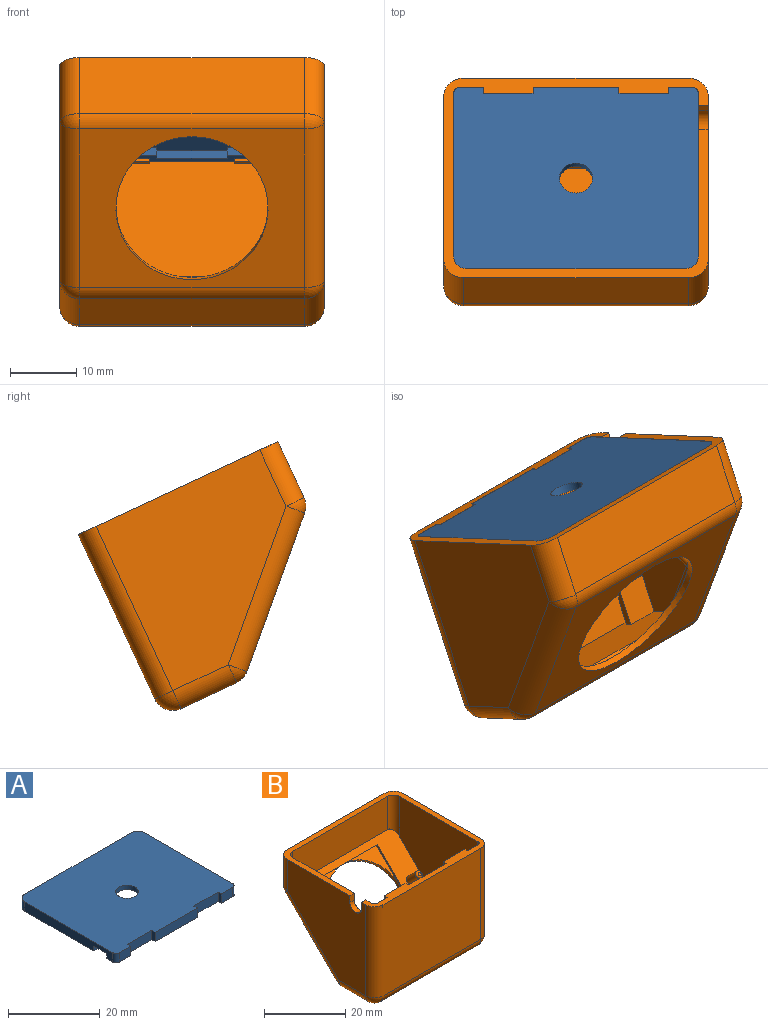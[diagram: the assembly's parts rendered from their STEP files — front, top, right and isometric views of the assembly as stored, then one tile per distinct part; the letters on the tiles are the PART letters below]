
ASSEMBLY  parts=2 mates=1
PART A: 37 faces, bbox 37x30.3x2.5 mm
  f0: plane 1.8x1.3mm, normal (1,0,0), area 2.3mm2, adj f17,f22,f33,f34
  f1: plane 33x2.5mm, normal (0,1,0), area 82.5mm2, adj f2,f16,f17,f18
  f2: cylinder r=2mm len=2.5mm, axis (0,0,1), area 7.9mm2, adj f1,f3,f17,f18
  f3: plane 27.3x2.5mm, normal (-1,0,0), area 63mm2, adj f2,f4,f17,f18,f33,f34,f35
  f4: cylinder r=1mm len=2.5mm, axis (0,0,1), area 3.9mm2, adj f3,f5,f17,f18
  f5: plane 3.5x2.5mm, normal (0,-1,0), area 8.7mm2, adj f4,f6,f17,f18
  f6: plane 2.5x1mm, normal (1,0,0), area 2.5mm2, adj f5,f7,f17,f18
  f7: plane 7.5x2.5mm, normal (0,-1,0), area 18.8mm2, adj f6,f8,f17,f18
  f8: plane 2.5x1mm, normal (-1,0,0), area 2.5mm2, adj f7,f9,f17,f18
  f9: plane 13x2.5mm, normal (0,-1,0), area 32.5mm2, adj f8,f10,f17,f18
  f10: plane 2.5x1mm, normal (1,0,0), area 2.5mm2, adj f9,f11,f17,f18
  f11: plane 7.5x2.5mm, normal (0,-1,0), area 18.8mm2, adj f10,f12,f17,f18
  f12: plane 2.5x1mm, normal (-1,0,0), area 2.5mm2, adj f11,f13,f17,f18
  f13: plane 3.5x2.5mm, normal (0,-1,0), area 8.7mm2, adj f12,f14,f17,f18
  f14: cylinder r=1mm len=2.5mm, axis (0,0,1), area 3.9mm2, adj f13,f15,f17,f18
  f15: plane 27.3x2.5mm, normal (1,0,0), area 68.2mm2, adj f14,f16,f17,f18
  f16: cylinder r=2mm len=2.5mm, axis (0,0,1), area 7.9mm2, adj f1,f15,f17,f18
  f17: plane 37x30.3mm, normal (0,0,-1), area 153.9mm2, adj f0,f1,f2,f3,f4,f5,f6,f7
  f18: plane 37x30.3mm, normal (0,0,1), area 1084.3mm2, adj f1,f2,f3,f4,f5,f6,f7,f8
  f19: plane 33x1.3mm, normal (0,-1,0), area 42.9mm2, adj f17,f20,f32,f33
  f20: cylinder r=0.8mm len=1.3mm, axis (0,0,1), area 1.6mm2, adj f17,f19,f21,f33
  f21: plane 21.3x1.3mm, normal (1,0,0), area 27.7mm2, adj f17,f20,f33,f35
  f22: plane 2.1x1.3mm, normal (0,1,0), area 2.7mm2, adj f0,f17,f23,f33
  f23: plane 1.3x1mm, normal (-1,0,0), area 1.3mm2, adj f17,f22,f24,f33
  f24: plane 9.9x1.3mm, normal (0,1,0), area 12.9mm2, adj f17,f23,f25,f33
  f25: plane 1.3x1mm, normal (1,0,0), area 1.3mm2, adj f17,f24,f26,f33
  f26: plane 10.6x1.3mm, normal (0,1,0), area 13.8mm2, adj f17,f25,f27,f33
  f27: plane 1.3x1mm, normal (-1,0,0), area 1.3mm2, adj f17,f26,f28,f33
  f28: plane 9.9x1.3mm, normal (0,1,0), area 12.9mm2, adj f17,f27,f29,f33
  f29: plane 1.3x1mm, normal (1,0,0), area 1.3mm2, adj f17,f28,f30,f33
  f30: plane 2.1x1.3mm, normal (0,1,0), area 2.7mm2, adj f17,f29,f31,f33
  f31: plane 27.1x1.3mm, normal (-1,0,0), area 35.2mm2, adj f17,f30,f32,f33
  f32: cylinder r=0.8mm len=1.3mm, axis (0,0,1), area 1.6mm2, adj f17,f19,f31,f33
  f33: plane 35.8x27.9mm, normal (0,0,-1), area 930.4mm2, adj f0,f3,f19,f20,f21,f22,f23,f24
  f34: plane 1.3x1.2mm, normal (0,1,0), area 1.6mm2, adj f0,f3,f17,f33
  f35: plane 1.3x1.2mm, normal (0,-1,0), area 1.6mm2, adj f3,f17,f21,f33
  f36: cylinder r=2.5mm len=5mm, axis (0,0,-1), area 18.8mm2, adj f18,f33
PART B: 68 faces, bbox 40x33.3x30.4 mm
  f0: plane 40x33.3mm, normal (0,0,1), area 214.3mm2, adj f2,f5,f8,f9,f10,f11,f12,f13
  f1: plane 37x11.38mm, normal (0,0,1), area 412.6mm2, adj f2,f4,f11,f13,f47,f48,f49,f50
  f2: plane 28.91x27.3mm, normal (1,0,0), area 626.6mm2, adj f0,f1,f4,f45,f48,f61,f63,f64
  f3: cylinder r=11.5mm len=23mm, axis (0,0.71,-0.71), area 72.3mm2, adj f7,f16,f19,f20,f21
  f4: plane 37x18.92mm, normal (0,-0.71,0.71), area 452.9mm2, adj f1,f2,f12,f13,f14,f15,f17,f18
  f5: plane 34x27.41mm, normal (0,-1,0), area 931.8mm2, adj f0,f38,f41,f44
  f6: plane 34x9.26mm, normal (0,0,-1), area 314.8mm2, adj f34,f39,f40,f44
  f7: plane 34x18.04mm, normal (0,0.71,-0.71), area 452mm2, adj f3,f29,f33,f34,f35
  f8: plane 34x9.36mm, normal (0,1,0), area 318.4mm2, adj f0,f28,f29,f30
  f9: plane 27.41x27.3mm, normal (1,0,0), area 585.4mm2, adj f0,f28,f33,f38,f39
  f10: plane 27.41x27.3mm, normal (-1,0,0), area 571.1mm2, adj f0,f30,f35,f40,f41,f63,f64,f65
  f11: plane 35x28.91mm, normal (0,1,0), area 968.1mm2, adj f0,f1,f53,f54,f55,f57,f58,f59
  f12: plane 33x9.99mm, normal (0,-1,0), area 329.5mm2, adj f0,f4,f45,f46
  f13: plane 28.91x27.3mm, normal (-1,0,0), area 640.9mm2, adj f0,f1,f4,f46,f51,f62,f66
  f14: plane 16.62x16.62mm, normal (-1,0,0), area 11.5mm2, adj f4,f15,f16,f17,f21
  f15: plane 23x0.35mm, normal (0,0.71,0.71), area 11.5mm2, adj f4,f14,f16,f18,f20
  f16: plane 11.5x8.13mm, normal (0,-0.71,0.71), area 28.4mm2, adj f3,f14,f15
  f17: plane 23x0.35mm, normal (0,-0.71,-0.71), area 11.5mm2, adj f4,f14,f18,f19,f21
  f18: plane 16.62x16.62mm, normal (1,0,0), area 11.5mm2, adj f4,f15,f17,f19,f20
  f19: plane 11.5x8.13mm, normal (0,-0.71,0.71), area 28.4mm2, adj f3,f17,f18
  f20: plane 11.5x8.13mm, normal (0,-0.71,0.71), area 28.4mm2, adj f3,f15,f18
  f21: plane 11.5x8.13mm, normal (0,-0.71,0.71), area 28.4mm2, adj f3,f14,f17
  f22: cylinder r=0.95mm len=4.53mm, axis (0,0.71,-0.71), area 26.9mm2, adj f4,f26
  f23: plane 0.9x0.64mm, normal (0,-0.71,0.71), area 0.6mm2, adj f26
  f24: cylinder r=0.95mm len=4.53mm, axis (0,0.71,-0.71), area 26.9mm2, adj f4,f27
  f25: plane 0.9x0.64mm, normal (0,-0.71,0.71), area 0.6mm2, adj f27
  f26: torus R=0.45mm, axis (0,-0.71,0.71), area 3.8mm2, adj f22,f23
  f27: torus R=0.45mm, axis (0,-0.71,0.71), area 3.8mm2, adj f24,f25
  f28: cylinder r=3mm len=9.36mm, axis (0,0,-1), area 44.1mm2, adj f0,f8,f9,f31
  f29: cylinder r=3mm len=34mm, axis (-1,0,0), area 80.1mm2, adj f7,f8,f31,f32
  f30: cylinder r=3mm len=9.36mm, axis (0,0,1), area 44.1mm2, adj f0,f8,f10,f32
  f31: sphere r=3mm, area 7.1mm2, adj f28,f29,f33
  f32: sphere r=3mm, area 7.1mm2, adj f29,f30,f35
  f33: cylinder r=3mm len=20.16mm, axis (0,-0.71,-0.71), area 120.2mm2, adj f7,f9,f31,f36
  f34: cylinder r=3mm len=34mm, axis (-1,0,0), area 80.1mm2, adj f6,f7,f36,f37
  f35: cylinder r=3mm len=20.16mm, axis (0,0.71,0.71), area 120.2mm2, adj f7,f10,f32,f37
  f36: sphere r=3mm, area 7.1mm2, adj f33,f34,f39
  f37: sphere r=3mm, area 7.1mm2, adj f34,f35,f40
  f38: cylinder r=3mm len=27.41mm, axis (0,0,1), area 129.1mm2, adj f0,f5,f9,f42
  f39: cylinder r=3mm len=9.26mm, axis (0,-1,0), area 43.6mm2, adj f6,f9,f36,f42
  f40: cylinder r=3mm len=9.26mm, axis (0,1,0), area 43.6mm2, adj f6,f10,f37,f43
  f41: cylinder r=3mm len=27.41mm, axis (0,0,-1), area 129.1mm2, adj f0,f5,f10,f43
  f42: sphere r=3mm, area 14.1mm2, adj f38,f39,f44
  f43: sphere r=3mm, area 14.1mm2, adj f40,f41,f44
  f44: cylinder r=3mm len=34mm, axis (-1,0,0), area 160.2mm2, adj f5,f6,f42,f43
  f45: cylinder r=2mm len=11.99mm, axis (0,0,-1), area 33.7mm2, adj f0,f2,f4,f12
  f46: cylinder r=2mm len=11.99mm, axis (0,0,1), area 33.7mm2, adj f0,f4,f12,f13
  f47: plane 5x3mm, normal (0,-1,0), area 15mm2, adj f1,f49,f61,f67
  f48: plane 6x5mm, normal (0,1,0), area 30mm2, adj f1,f2,f49,f61
  f49: plane 6x1mm, normal (1,0,0), area 5mm2, adj f1,f47,f48,f61
  f50: plane 3x3mm, normal (0,-1,0), area 9mm2, adj f1,f52,f62,f66
  f51: plane 6x3mm, normal (0,1,0), area 18mm2, adj f1,f13,f52,f62
  f52: plane 6x1mm, normal (-1,0,0), area 5mm2, adj f1,f50,f51,f62
  f53: plane 2.91x1mm, normal (1,0,0), area 2.9mm2, adj f0,f11,f54,f56
  f54: plane 7.5x1mm, normal (0,0,-1), area 7.5mm2, adj f11,f53,f55,f56
  f55: plane 2.91x1mm, normal (-1,0,0), area 2.9mm2, adj f0,f11,f54,f56
  f56: plane 7.5x2.91mm, normal (0,1,0), area 21.8mm2, adj f0,f53,f54,f55
  f57: plane 2.91x1mm, normal (1,0,0), area 2.9mm2, adj f0,f11,f58,f60
  f58: plane 7.5x1mm, normal (0,0,-1), area 7.5mm2, adj f11,f57,f59,f60
  f59: plane 2.91x1mm, normal (-1,0,0), area 2.9mm2, adj f0,f11,f58,f60
  f60: plane 7.5x2.91mm, normal (0,1,0), area 21.8mm2, adj f0,f57,f58,f59
  f61: cylinder r=5mm len=5mm, axis (1,0,0), area 16.1mm2, adj f2,f47,f48,f49
  f62: cylinder r=5mm len=3mm, axis (1,0,0), area 9.7mm2, adj f13,f50,f51,f52
  f63: plane 2x1.5mm, normal (0,1,0), area 3mm2, adj f0,f2,f10,f64
  f64: cylinder r=2mm len=4mm, axis (1,0,0), area 9.4mm2, adj f2,f10,f63,f65
  f65: plane 2x1.5mm, normal (0,-1,0), area 3mm2, adj f0,f2,f10,f64
  f66: cylinder r=1mm len=28.91mm, axis (0,0,-1), area 45.4mm2, adj f0,f1,f11,f13,f50
  f67: cylinder r=1mm len=28.91mm, axis (0,0,1), area 45.4mm2, adj f0,f1,f2,f11,f47
PLACE A rot(axis=(0,0.22,0.98),180deg) t=(13.38,18.07,-9.55)mm
PLACE B rot(axis=(0,0.22,0.98),180deg) t=(62.23,18.09,-9.51)mm
MATE slider A.f18 <-> B.f0  axis (0,0.42,0.91) through (35.73,15.81,-8.49)mm
